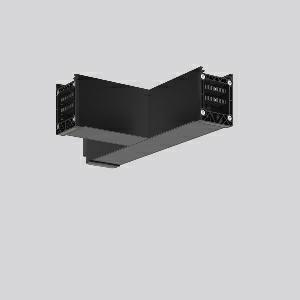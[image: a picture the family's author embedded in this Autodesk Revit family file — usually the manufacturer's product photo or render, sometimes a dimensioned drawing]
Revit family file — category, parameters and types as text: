
# Revit family: linedo_t-verbindung_982774_003_1_babb
name_source: partatom
category: Lighting Fixtures
units: mm (PartAtom-declared; Revit-internal decimal feet)

## family parameters
Cut with Voids When Loaded = No
Host = Face
Light Source = No
Part Type = Normal
Room Calculation Point = No
Round Connector Dimension = Use Diameter
Shared = No

## types (1)
- LINEDO T-Verbindung
    Apparent Load = 0 VA
    Default Elevation = 1800 mm
    Description = Series: LINEDO
T-connector, 14-pole, connection socket / plug - socket. Housing: extruded aluminium profile, powder-coated. Cover made of plastic, surface like housing. LINEDO plug system, plastic, black. Easy connection for rigid or flexible wires. 5 membrane cable entries (2 x M20 and 3 x M25). Suitable for power supply in 7-pole version. Ready prewired. Colour-coded individual cables enable easy electromechanical separation.
Colour: jet black (RAL 9005)
Length: 330 mm
Width: 185 mm
Height: 76 mm
Weight: 1070 g
    Height = 76 mm
    Lamp = 0 x
    Length = 331 mm
    Luminous efficacy = 0 lm/W
    Manufacturer = RZB
    ModVariant = No
    Model = 982774.003.1
    Mounting Place = Ceiling
    Mounting Type = Surface mounted
    Number of Poles = 1
    OnlyDefault = Yes
    Power Factor = 1
    Product Name = LINEDO T-Verbindung
    Product group = Surface mounted continuous line luminaire system
    ProductGroupID = 310
    Protection Class = Protection class I
    Protection Degree = Degree of protection
    RLX_Detail_Level = 1
    RLX_Emergency_Light_Flux = 0 lm
    RLX_Emergency_Type = 0
    RLX_Emergency_Type_DB = No
    RlxData = <blob elided: 19897 chars, md5=bce78855>
    Standby Power = 0 W
    System Light Flux = 0 lm
    System Power = 0 W
    Type Comments = Product without accessories
    Type Image = 982774.003.1.jpg
    URL = http://relux.com
    VarID = ---
    Voltage = 0 V
    Weight = 0.00 kg
    Width = 185 mm

## geometry (parser evidence)
native form markers: Blend x4, Sweep x12
no freeform markers — native parametric forms only
